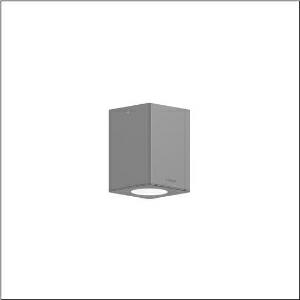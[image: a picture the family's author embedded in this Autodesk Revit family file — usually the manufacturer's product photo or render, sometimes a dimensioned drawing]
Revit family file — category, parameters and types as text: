
# Revit family: cl_31_decke_5cl613603
name_source: partatom
category: Lighting Fixtures
units: mm (PartAtom-declared; Revit-internal decimal feet)

## family parameters
Cut with Voids When Loaded = No
Host = Face
Light Source = No
Part Type = Normal
Room Calculation Point = No
Round Connector Dimension = Use Diameter
Shared = No

## types (1)
- --- (1 x LED, 1500 lm, 15 W, 3000K)
    Apparent Load = 15 VA
    CIE Flux Codes = 98 100 100 100 100
    Color Rendering = 80
    Color Temperature = 3000K
    Default Elevation = 1800 mm
    Description = CL 31 Ceiling, ceiling luminaire, primary light control with reflector, of aluminium, primary optical cover: cover panel, of glass, transparent, primary light characteristic: symmetric, installation type: surface-mounted, LED, rated luminous flux: 1.500lm, luminous efficacy: 100lm/W, light colour: 830, colour temperature: 3000K, control gear: DALI, with terminal, 5-pole, max. 2.5mm², mains connection: 220..240V, AC, 50/60Hz, rated input power: 15W, luminaire housing, of aluminium, powder-coated, Siteco® metallic grey, length: 120mm, width: 120mm, height: 165mm, protection rating (complete): IP65, insulation class (complete): insulation class I (protective earthing), certification: CE, ENEC, impact resistance: IK09, permissible operating ambient temperature for outdoor applications: -20..+50°C, packaging unit: 1 piece
    Height = 166 mm
    Lamp = 1 x LED
    Lamp Light Flux = 1500 lm
    Lamp Power = 15 W
    Lamp count = 1
    Length = 120 mm
    Luminous efficacy = 100 lm/W
    Manufacturer = Siteco
    ModVariant = No
    Model = 5CL613603
    Mounting Place = Ceiling
    Mounting Type = Surface mounted
    Number of Poles = 1
    OnlyDefault = Yes
    Power Factor = 1
    Product Name = CL 31 Decke
    Product group = ceiling luminaire
    ProductGroupID = 308
    Protection Class = Protection class I
    Protection Degree = IP 65
    RLX_Detail_Level = 1
    RLX_Emergency_Light_Flux = 0 lm
    RLX_Emergency_Type = 0
    RLX_Emergency_Type_DB = No
    RlxData = <blob elided: 33341 chars, md5=d0c4343b>
    Socket = socket
    Standby Power = 0 W
    System Light Flux = 1500 lm
    System Power = 15 W
    Type Comments = factory setting: luminous flux: 100 % | dim-lin: 254 | 348 mA
    Type Image = l_1006909.jpg
    URL = http://relux.com
    VarID = @adj_216777
    Voltage = 0 V
    Weight = 0.00 kg
    Width = 120 mm

## geometry (parser evidence)
native form markers: Blend x4, Sweep x11
no freeform markers — native parametric forms only
